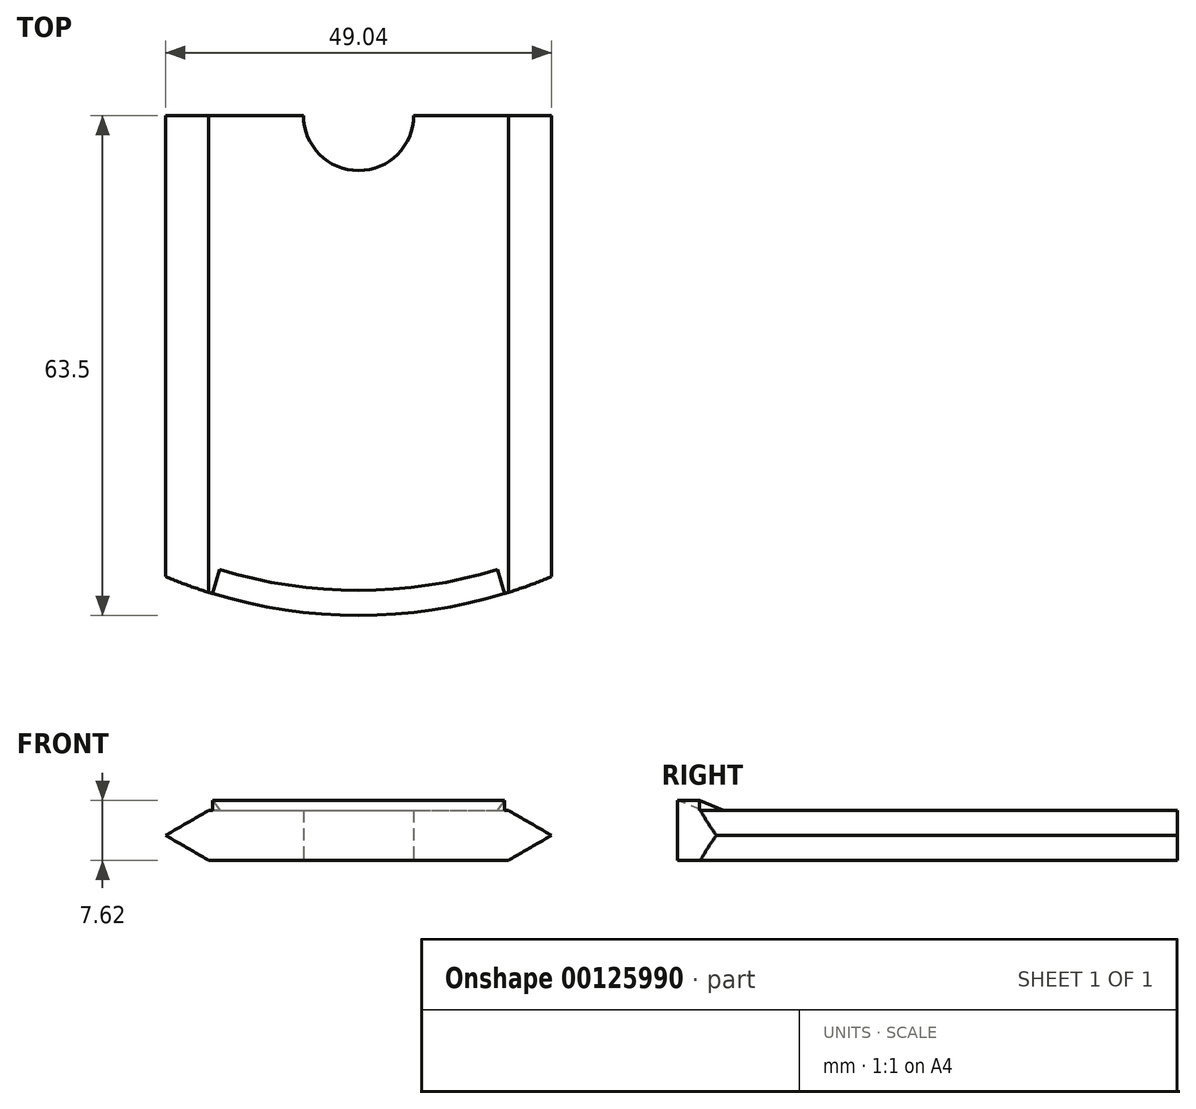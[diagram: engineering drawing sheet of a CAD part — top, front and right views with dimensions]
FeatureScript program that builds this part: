
annotation { "Feature Type Name" : "Feature", "Feature Type Description" : "" }
export const myFeature = defineFeature(function(context is Context, id is Id, definition is map)
    precondition{}
    {
        {
            var Q0;
            Q0=qCreatedBy(makeId("Top.planeOp"),FACE);
            var sketch = newSketch(context, id + "F0", { "sketchPlane" : qUnion([Q0])});
            skLineSegment(sketch, "E0.bottom", {"start": v(-19.05, 0) * mm, "end": v(19.05, 0) * mm});
            skLineSegment(sketch, "E0.top", {"start": v(-19.05, -69.85) * mm, "end": v(19.05, -69.85) * mm});
            skLineSegment(sketch, "E0.left", {"start": v(-19.05, 0) * mm, "end": v(-19.05, -69.85) * mm});
            skLineSegment(sketch, "E0.right", {"start": v(19.05, 0) * mm, "end": v(19.05, -69.85) * mm});
            skCircle(sketch, "E1", {"center": v(0, 0) * mm, "radius": 7 * mm});
            skCircle(sketch, "E2", {"center": v(0, 0) * mm, "radius": 63.5 * mm});
            skLineSegment(sketch, "E3.bottom", {"start": v(-25.4, 0) * mm, "end": v(25.4, 0) * mm});
            skLineSegment(sketch, "E3.top", {"start": v(-25.4, -74.3) * mm, "end": v(25.4, -74.3) * mm});
            skLineSegment(sketch, "E3.left", {"start": v(-25.4, 0) * mm, "end": v(-25.4, -74.3) * mm});
            skLineSegment(sketch, "E3.right", {"start": v(25.4, 0) * mm, "end": v(25.4, -74.3) * mm});
            skSolve(sketch);
        }
        {
            var Q0;
            {var subQ1=sQuery(id+"F0.wireOp",EDGE,"E0.left");var subQ5=sQuery(id+"F0.wireOp",EDGE,"E3.bottom");var subQ6=makeQuery(id+"F0.imprint","INTERSECT",VERTEX,{"derivedFrom":[subQ1,subQ5]});Q0=makeQuery(id+"F0.imprint","IMPRINT",FACE,{"disambiguationData":[TD([[makeQuery(id+"F0.imprint","IMPRINT",EDGE,{"disambiguationData":[TD([[subQ6,-1.0]])],"derivedFrom":subQ1}),1.0]])]});}
            var Q1;
            {var subQ0=sQuery(id+"F0.wireOp",EDGE,"E3.bottom");var subQ1=sQuery(id+"F0.wireOp",EDGE,"E0.right");var subQ2=makeQuery(id+"F0.imprint","INTERSECT",VERTEX,{"derivedFrom":[subQ1,subQ0]});Q1=makeQuery(id+"F0.imprint","IMPRINT",FACE,{"disambiguationData":[TD([[makeQuery(id+"F0.imprint","IMPRINT",EDGE,{"disambiguationData":[TD([[subQ2,-1.0]])],"derivedFrom":subQ1}),1.0]])]});}
            var Q2;
            {var subQ0=sQuery(id+"F0.wireOp",EDGE,"E3.bottom");var subQ1=sQuery(id+"F0.wireOp",EDGE,"E0.left");var subQ2=makeQuery(id+"F0.imprint","INTERSECT",VERTEX,{"derivedFrom":[subQ1,subQ0]});Q2=makeQuery(id+"F0.imprint","IMPRINT",FACE,{"disambiguationData":[TD([[makeQuery(id+"F0.imprint","IMPRINT",EDGE,{"disambiguationData":[TD([[subQ2,-1.0]])],"derivedFrom":subQ1}),-1.0]])]});}
            extrude(context, id + "F1", {"entities" : qUnion([Q0, Q1, Q2]), "offsetDistance" : 25 * mm, "depth" : 6.35 * mm});
        }
        {
            var Q0;
            {var subQ0=sQuery(id+"F0.wireOp",EDGE,"E3.bottom");var subQ1=makeQuery(id+"F0.imprint","INTERSECT",VERTEX,{"derivedFrom":[sQuery(id+"F0.wireOp",EDGE,"E0.left"),subQ0]});Q0=makeQuery(id+"F1.opExtrude","SWEPT_FACE",FACE,{"disambiguationData":[OSD([subQ0]),TDD([makeQuery(id+"F0.imprint","IMPRINT",EDGE,{"disambiguationData":[TD([[subQ1,1.0]])],"derivedFrom":subQ0}),makeQuery(id+"F0.imprint","IMPRINT",EDGE,{"disambiguationData":[TD([[subQ1,-1.0]])],"derivedFrom":subQ0})])]});}
            var sketch = newSketch(context, id + "F2", { "sketchPlane" : qUnion([Q0])});
            skLineSegment(sketch, "E4", {"start": v(19.02, 0) * mm, "end": v(24.52, 3.17) * mm});
            skLineSegment(sketch, "E5", {"start": v(24.52, 3.17) * mm, "end": v(19.02, 6.35) * mm});
            skLineSegment(sketch, "E6", {"start": v(19.02, 6.35) * mm, "end": v(19.02, 0) * mm});
            skSolve(sketch);
        }
        {
            var Q0;
            {var subQ7=sQuery(id+"F2.wireOp",EDGE,"E4");Q0=makeQuery(id+"F2.imprint","IMPRINT",FACE,{"disambiguationData":[TD([[makeQuery(id+"F2.imprint","IMPRINT",EDGE,{"derivedFrom":subQ7}),-1.0]])]});}
            extrude(context, id + "F3", {"entities" : qUnion([Q0]), "operationType" : NewBodyOperationType.REMOVE, "oppositeDirection" : true, "offsetDistance" : 25 * mm, "depth" : 76.2 * mm});
        }
        {
            var Q0;
            {var subQ0=sQuery(id+"F0.wireOp",EDGE,"E3.bottom");var subQ1=makeQuery(id+"F0.imprint","INTERSECT",VERTEX,{"derivedFrom":[sQuery(id+"F0.wireOp",EDGE,"E0.right"),subQ0]});Q0=makeQuery(id+"F1.opExtrude","SWEPT_FACE",FACE,{"disambiguationData":[OSD([subQ0]),TDD([makeQuery(id+"F0.imprint","IMPRINT",EDGE,{"disambiguationData":[TD([[subQ1,1.0]])],"derivedFrom":subQ0}),makeQuery(id+"F0.imprint","IMPRINT",EDGE,{"disambiguationData":[TD([[subQ1,-1.0]])],"derivedFrom":subQ0})])]});}
            var sketch = newSketch(context, id + "F4", { "sketchPlane" : qUnion([Q0])});
            skLineSegment(sketch, "E7", {"start": v(-19.02, 6.35) * mm, "end": v(-24.52, 3.18) * mm});
            skLineSegment(sketch, "E8", {"start": v(-24.52, 3.18) * mm, "end": v(-19.02, 0) * mm});
            skLineSegment(sketch, "E9", {"start": v(-19.02, 6.35) * mm, "end": v(-19.02, 0) * mm});
            skSolve(sketch);
        }
        {
            var Q0;
            {var subQ8=sQuery(id+"F4.wireOp",EDGE,"E7");Q0=makeQuery(id+"F4.imprint","IMPRINT",FACE,{"disambiguationData":[TD([[makeQuery(id+"F4.imprint","IMPRINT",EDGE,{"derivedFrom":subQ8}),-1.0]])]});}
            extrude(context, id + "F5", {"entities" : qUnion([Q0]), "operationType" : NewBodyOperationType.REMOVE, "oppositeDirection" : true, "depth" : 76.2 * mm});
        }
        {
            var Q0;
            Q0=makeQuery(id+"F1.opExtrude","CAP_FACE",FACE,{"disambiguationData":[OSD([sQuery(id+"F0.wireOp",EDGE,"E1"),sQuery(id+"F0.wireOp",EDGE,"E2"),sQuery(id+"F0.wireOp",EDGE,"E3.bottom"),sQuery(id+"F0.wireOp",EDGE,"E3.left"),sQuery(id+"F0.wireOp",EDGE,"E3.right")])],"isStart":false});
            var sketch = newSketch(context, id + "F6", { "sketchPlane" : qUnion([Q0])});
            skCircle(sketch, "E10", {"center": v(0, 0) * mm, "radius": 60.33 * mm});
            skCircle(sketch, "E11", {"center": v(0, 0) * mm, "radius": 63.5 * mm});
            skSolve(sketch);
        }
        {
            var Q0;
            Q0=qCreatedBy(makeId("Right.planeOp"),FACE);
            var sketch = newSketch(context, id + "F7", { "sketchPlane" : qUnion([Q0])});
            skLineSegment(sketch, "E12", {"start": v(-63.5, 6.35) * mm, "end": v(-63.5, 7.62) * mm});
            skLineSegment(sketch, "E13", {"start": v(-63.5, 7.62) * mm, "end": v(-60.33, 6.35) * mm});
            skLineSegment(sketch, "E14", {"start": v(-60.33, 6.35) * mm, "end": v(-63.5, 6.35) * mm});
            skSolve(sketch);
        }
        {
            var Q0;
            Q0=makeQuery(id+"F7.imprint","IMPRINT",FACE,{"disambiguationData":[TD([[makeQuery(id+"F7.imprint","IMPRINT",EDGE,{"derivedFrom":sQuery(id+"F7.wireOp",EDGE,"E12")}),-1.0]])]});
            var Q1;
            Q1=makeQuery(id+"F1.opExtrude","SWEPT_FACE",FACE,{"disambiguationData":[OSD([sQuery(id+"F0.wireOp",EDGE,"E2")])]});
            revolve(context, id + "F8", {"operationType" : NewBodyOperationType.ADD, "surfaceOperationType" : NewSurfaceOperationType.NEW, "entities" : qUnion([Q0]), "axis" : qUnion([Q1]), "revolveType" : RevolveType.SYMMETRIC, "angle" : 34 * degree});
        }
    });
